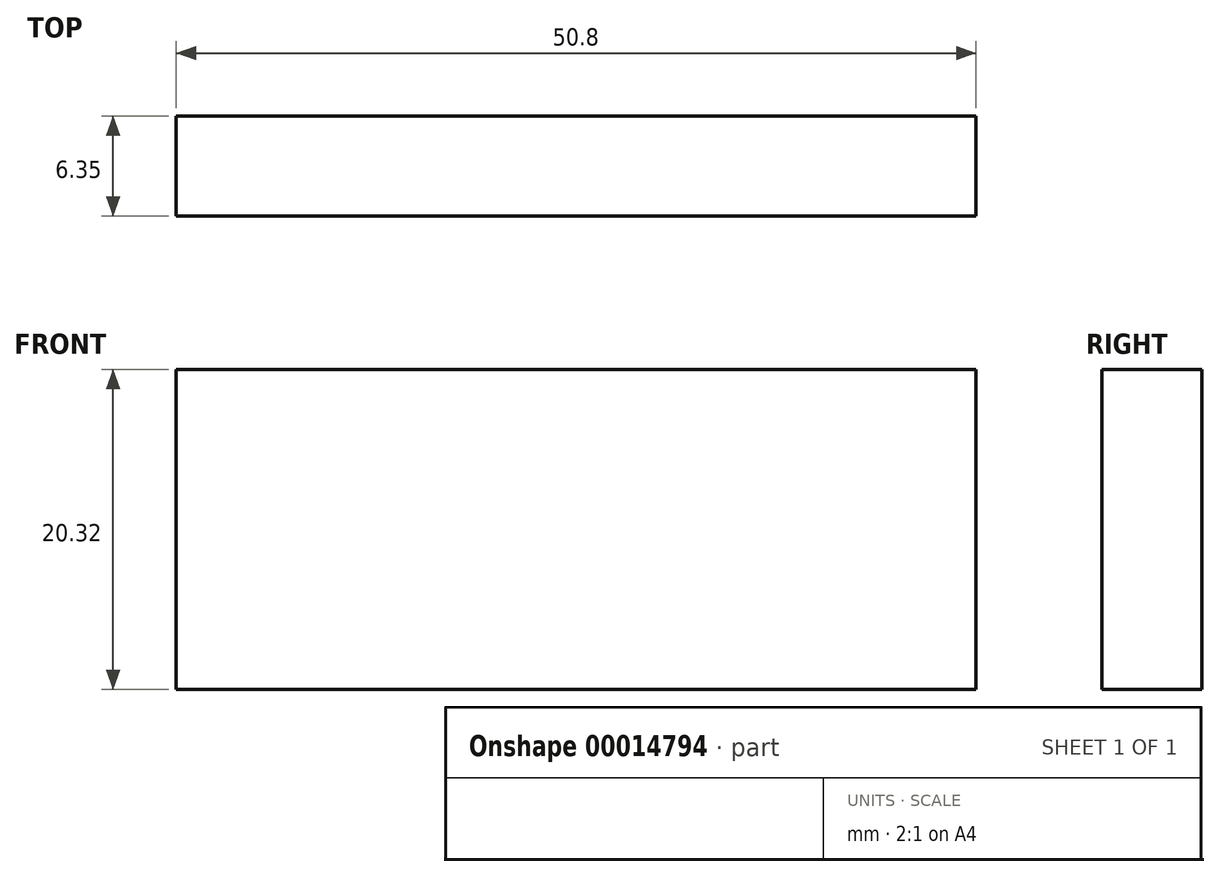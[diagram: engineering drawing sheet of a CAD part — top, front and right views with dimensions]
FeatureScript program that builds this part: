
annotation { "Feature Type Name" : "Feature", "Feature Type Description" : "" }
export const myFeature = defineFeature(function(context is Context, id is Id, definition is map)
    precondition{}
    {
        {
            var Q0;
            Q0=qCreatedBy(makeId("Front.planeOp"),FACE);
            var sketch = newSketch(context, id + "F0", { "sketchPlane" : qUnion([Q0])});
            skLineSegment(sketch, "E0.rect.bottom", {"start": v(25.4, -10.16) * mm, "end": v(-25.4, -10.16) * mm});
            skLineSegment(sketch, "E0.rect.top", {"start": v(25.4, 10.16) * mm, "end": v(-25.4, 10.16) * mm});
            skLineSegment(sketch, "E0.rect.left", {"start": v(25.4, -10.16) * mm, "end": v(25.4, 10.16) * mm});
            skLineSegment(sketch, "E0.rect.right", {"start": v(-25.4, -10.16) * mm, "end": v(-25.4, 10.16) * mm});
            skPoint(sketch, "E0.rect.middle", {"position": v(0, 0) * mm});
            skSolve(sketch);
        }
        {
            var Q0;
            Q0 = qSketchRegion(id + "F0", true);
            extrude(context, id + "F1", {"entities" : qUnion([Q0]), "depth" : 6.35 * mm});
        }
    });
